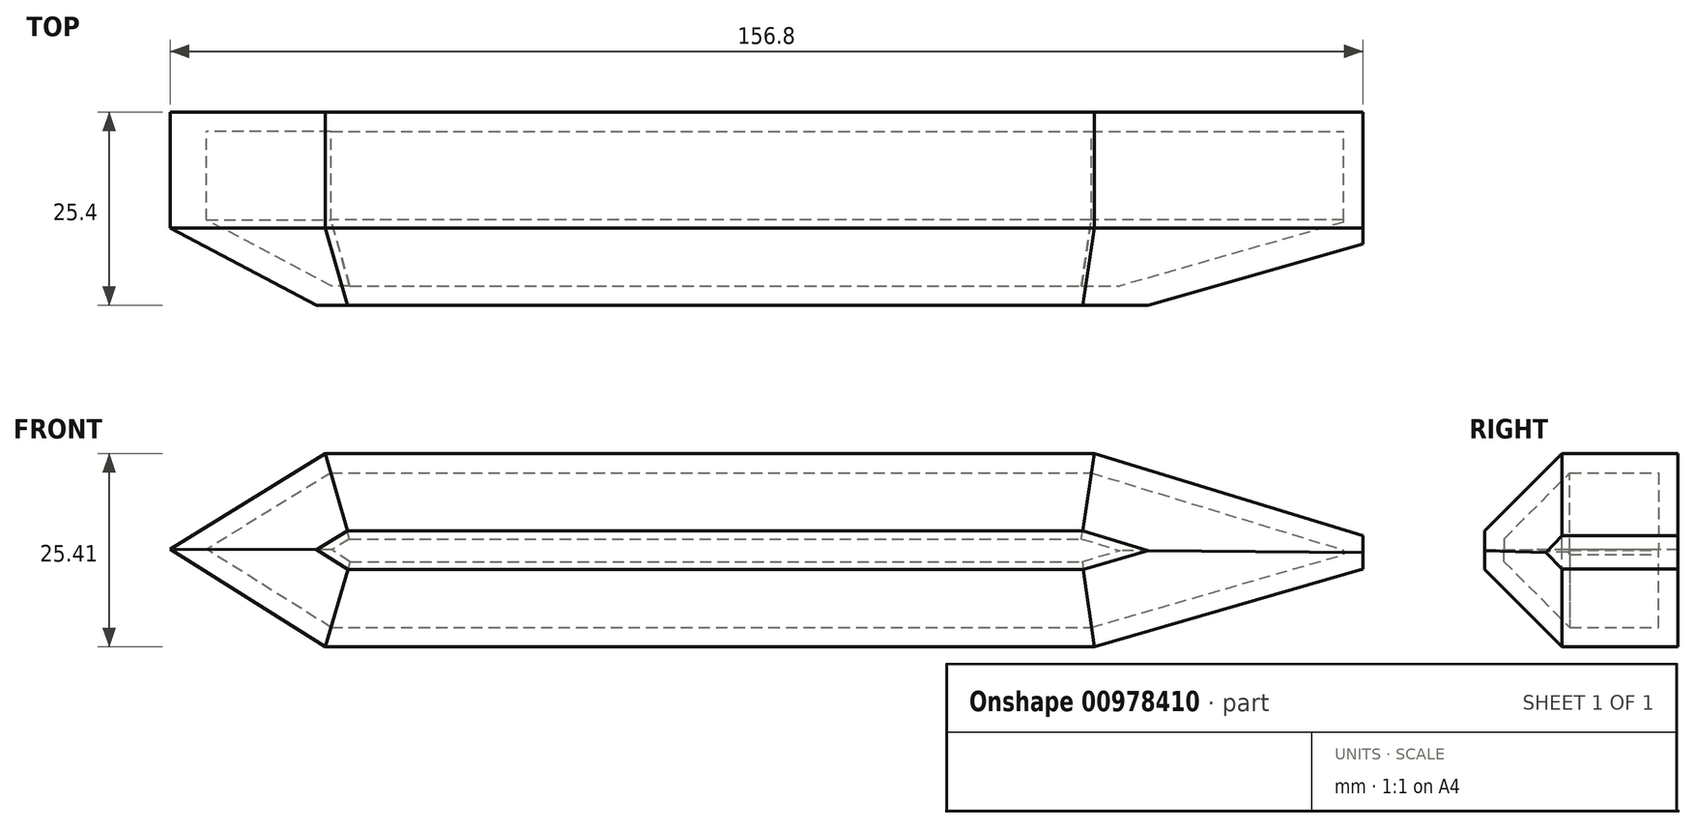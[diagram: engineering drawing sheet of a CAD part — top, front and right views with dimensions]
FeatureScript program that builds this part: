
annotation { "Feature Type Name" : "Feature", "Feature Type Description" : "" }
export const myFeature = defineFeature(function(context is Context, id is Id, definition is map)
    precondition{}
    {
        {
            var Q0;
            Q0=qCreatedBy(makeId("Front.planeOp"),FACE);
            var sketch = newSketch(context, id + "F0", { "sketchPlane" : qUnion([Q0])});
            skLineSegment(sketch, "E0.bottom", {"start": v(-60.88, -19.13) * mm, "end": v(40.15, -19.13) * mm});
            skLineSegment(sketch, "E0.top", {"start": v(-60.88, 6.28) * mm, "end": v(40.15, 6.28) * mm});
            skLineSegment(sketch, "E0.left", {"start": v(-60.88, -19.13) * mm, "end": v(-60.88, 6.28) * mm});
            skLineSegment(sketch, "E0.right", {"start": v(40.15, -19.13) * mm, "end": v(40.15, 6.28) * mm});
            skLineSegment(sketch, "E1", {"start": v(40.15, 6.28) * mm, "end": v(75.48, -4.53) * mm});
            skLineSegment(sketch, "E2", {"start": v(40.15, -19.13) * mm, "end": v(75.48, -8.9) * mm});
            skLineSegment(sketch, "E3", {"start": v(75.48, -8.9) * mm, "end": v(75.48, -4.53) * mm});
            skLineSegment(sketch, "E4", {"start": v(-60.88, 6.28) * mm, "end": v(-81.32, -6.28) * mm});
            skLineSegment(sketch, "E5", {"start": v(-60.88, -19.13) * mm, "end": v(-81.32, -6.28) * mm});
            skSolve(sketch);
        }
        {
            var Q0;
            Q0=makeQuery(id+"F0.imprint","IMPRINT",FACE,{"disambiguationData":[TD([[makeQuery(id+"F0.imprint","IMPRINT",EDGE,{"derivedFrom":sQuery(id+"F0.wireOp",EDGE,"E0.bottom")}),1.0]])]});
            var Q1;
            Q1=makeQuery(id+"F0.imprint","IMPRINT",FACE,{"disambiguationData":[TD([[makeQuery(id+"F0.imprint","IMPRINT",EDGE,{"derivedFrom":sQuery(id+"F0.wireOp",EDGE,"E0.left")}),1.0]])]});
            var Q2;
            Q2=makeQuery(id+"F0.imprint","IMPRINT",FACE,{"disambiguationData":[TD([[makeQuery(id+"F0.imprint","IMPRINT",EDGE,{"derivedFrom":sQuery(id+"F0.wireOp",EDGE,"E0.right")}),-1.0]])]});
            extrude(context, id + "F1", {"entities" : qUnion([Q0, Q1, Q2]), "depth" : 25.4 * mm, "offsetDistance" : 25.4 * mm});
        }
        {
            var Q0;
            Q0=makeQuery(id+"F1.opExtrude","CAP_EDGE",EDGE,{"disambiguationData":[OSD([sQuery(id+"F0.wireOp",EDGE,"E0.top")])],"isStart":false});
            var Q1;
            Q1=makeQuery(id+"F1.opExtrude","CAP_EDGE",EDGE,{"disambiguationData":[OSD([sQuery(id+"F0.wireOp",EDGE,"E4")])],"isStart":false});
            var Q2;
            Q2=makeQuery(id+"F1.opExtrude","CAP_EDGE",EDGE,{"disambiguationData":[OSD([sQuery(id+"F0.wireOp",EDGE,"E1")])],"isStart":false});
            var Q3;
            Q3=makeQuery(id+"F1.opExtrude","CAP_EDGE",EDGE,{"disambiguationData":[OSD([sQuery(id+"F0.wireOp",EDGE,"E5")])],"isStart":false});
            var Q4;
            Q4=makeQuery(id+"F1.opExtrude","CAP_EDGE",EDGE,{"disambiguationData":[OSD([sQuery(id+"F0.wireOp",EDGE,"E2")])],"isStart":false});
            var Q5;
            Q5=makeQuery(id+"F1.opExtrude","CAP_EDGE",EDGE,{"disambiguationData":[OSD([sQuery(id+"F0.wireOp",EDGE,"E0.bottom")])],"isStart":false});
            var Q6;
            Q6=makeQuery(id+"F1.opExtrude","CAP_EDGE",EDGE,{"disambiguationData":[OSD([sQuery(id+"F0.wireOp",EDGE,"E3")])],"isStart":false});
            chamfer(context, id + "F2", {"entities" : qUnion([Q0, Q1, Q2, Q3, Q4, Q5, Q6]), "width" : 10.16 * mm, "tangentPropagation" : true});
        }
        {
            var Q0;
            Q0=makeQuery(id+"F1.opExtrude","CAP_FACE",FACE,{"disambiguationData":[OSD([sQuery(id+"F0.wireOp",EDGE,"E0.bottom"),sQuery(id+"F0.wireOp",EDGE,"E0.top"),sQuery(id+"F0.wireOp",EDGE,"E1"),sQuery(id+"F0.wireOp",EDGE,"E2"),sQuery(id+"F0.wireOp",EDGE,"E3"),sQuery(id+"F0.wireOp",EDGE,"E4"),sQuery(id+"F0.wireOp",EDGE,"E5")])],"isStart":true});
            var Q1;
            Q1=makeQuery(id+"F1.opExtrude","SWEPT_BODY",BODY,{"disambiguationData":[OSD([sQuery(id+"F0.wireOp",EDGE,"E0.bottom"),sQuery(id+"F0.wireOp",EDGE,"E0.top"),sQuery(id+"F0.wireOp",EDGE,"E1"),sQuery(id+"F0.wireOp",EDGE,"E2"),sQuery(id+"F0.wireOp",EDGE,"E3"),sQuery(id+"F0.wireOp",EDGE,"E4"),sQuery(id+"F0.wireOp",EDGE,"E5")])]});
            shell(context, id + "F3", {"isHollow" : true, "entities" : qUnion([Q0]), "parts" : qUnion([Q1]), "thickness" : 2.54 * mm});
        }
    });
